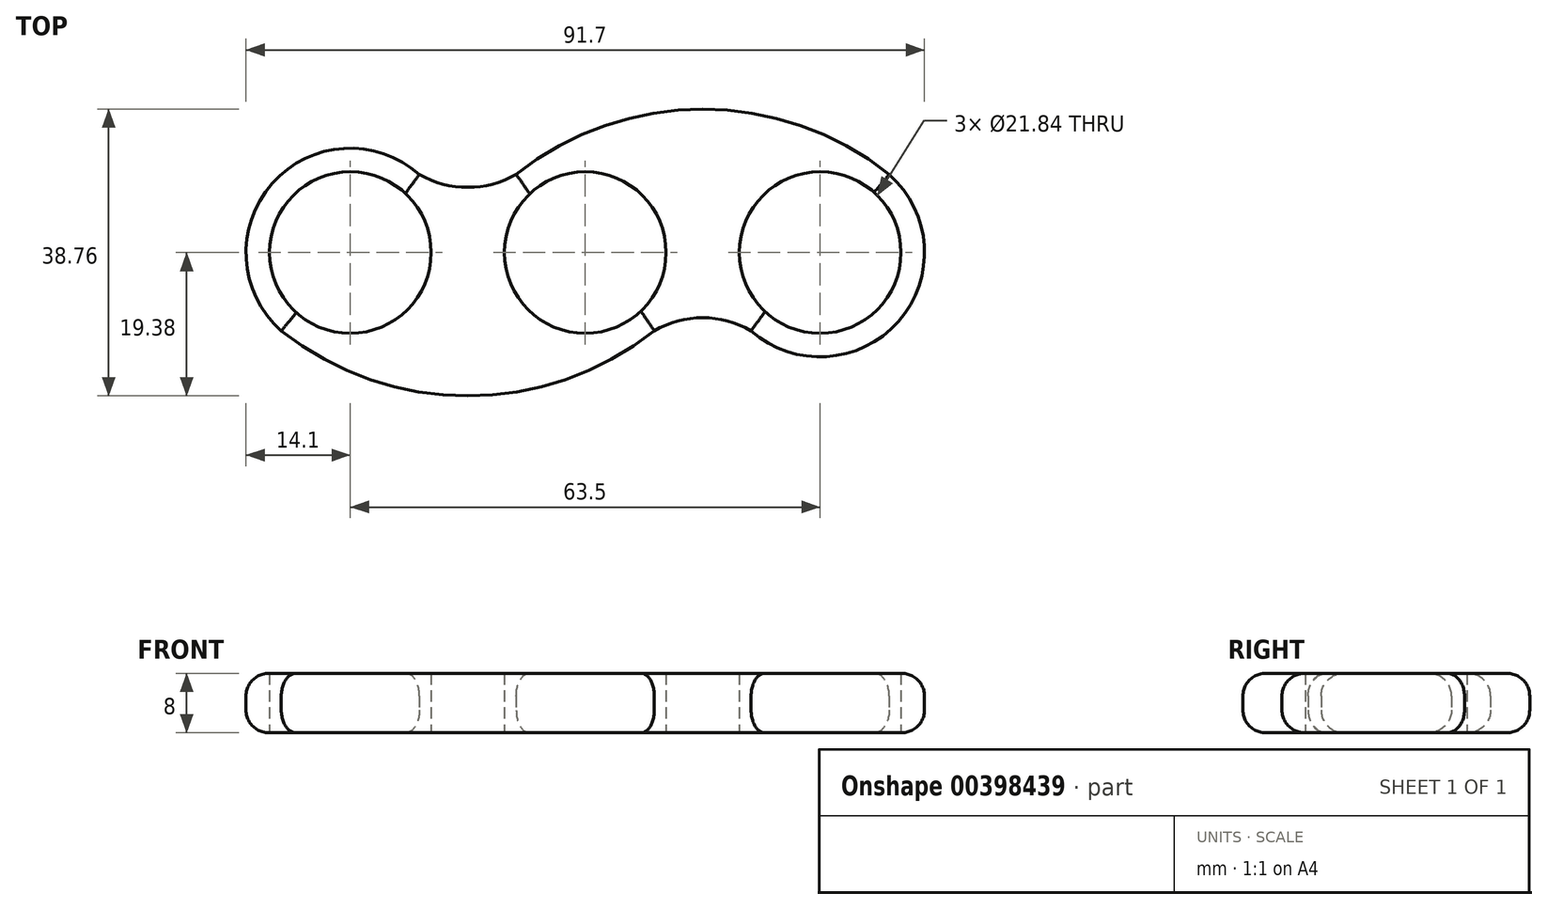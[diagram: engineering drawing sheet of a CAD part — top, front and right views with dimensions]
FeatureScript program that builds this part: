
annotation { "Feature Type Name" : "Feature", "Feature Type Description" : "" }
export const myFeature = defineFeature(function(context is Context, id is Id, definition is map)
    precondition{}
    {
        {
            var Q0;
            Q0=qCreatedBy(makeId("Top.planeOp"),FACE);
            var sketch = newSketch(context, id + "F0", { "sketchPlane" : qUnion([Q0])});
            skCircle(sketch, "E0", {"center": v(0, 0) * mm, "radius": 10.92 * mm});
            skCircle(sketch, "E1", {"center": v(0, 0) * mm, "radius": 14.1 * mm});
            skLineSegment(sketch, "E2", {"start": v(0, 0) * mm, "end": v(-31.75, 0) * mm});
            skLineSegment(sketch, "E3", {"start": v(0, 0) * mm, "end": v(31.75, 0) * mm});
            skCircle(sketch, "E4", {"center": v(31.75, 0) * mm, "radius": 10.92 * mm});
            skCircle(sketch, "E5", {"center": v(31.75, 0) * mm, "radius": 14.1 * mm});
            skCircle(sketch, "E6", {"center": v(-31.75, 0) * mm, "radius": 10.92 * mm});
            skCircle(sketch, "E7", {"center": v(-31.75, 0) * mm, "radius": 14.1 * mm});
            skPoint(sketch, "E8", {"position": v(-15.88, 0) * mm});
            skPoint(sketch, "E9", {"position": v(15.88, 0) * mm});
            skPoint(sketch, "E10", {"position": v(-15.88, 8.81) * mm});
            skPoint(sketch, "E11", {"position": v(15.88, -8.81) * mm});
            skPoint(sketch, "E12", {"position": v(-9.32, 10.57) * mm});
            skPoint(sketch, "E13", {"position": v(-22.42, 10.57) * mm});
            skArc(sketch, "E14", {"start": v(-22.42, 10.57) * mm, "mid": v(-15.87, 8.81) * mm, "end": v(-9.32, 10.57) * mm});
            skPoint(sketch, "E15", {"position": v(-41.08, -10.57) * mm});
            skPoint(sketch, "E16", {"position": v(9.33, -10.57) * mm});
            skPoint(sketch, "E17", {"position": v(41.08, 10.57) * mm});
            skPoint(sketch, "E18", {"position": v(22.42, -10.57) * mm});
            skArc(sketch, "E19", {"start": v(22.42, -10.57) * mm, "mid": v(15.88, -8.81) * mm, "end": v(9.33, -10.57) * mm});
            skPoint(sketch, "E20", {"position": v(-15.88, -19.38) * mm});
            skPoint(sketch, "E21", {"position": v(15.87, 19.38) * mm});
            skArc(sketch, "E22", {"start": v(-41.08, -10.57) * mm, "mid": v(-15.88, -19.38) * mm, "end": v(9.33, -10.57) * mm});
            skArc(sketch, "E23", {"start": v(41.08, 10.57) * mm, "mid": v(15.88, 19.38) * mm, "end": v(-9.32, 10.57) * mm});
            skSolve(sketch);
        }
        {
            var Q0;
            Q0=makeQuery(id+"F0.imprint","IMPRINT",FACE,{"disambiguationData":[TD([[makeQuery(id+"F0.imprint","IMPRINT",EDGE,{"derivedFrom":sQuery(id+"F0.wireOp",EDGE,"E6")}),-1.0]])]});
            var Q1;
            {var subQ0=sQuery(id+"F0.wireOp",EDGE,"E14");Q1=makeQuery(id+"F0.imprint","IMPRINT",FACE,{"disambiguationData":[TD([[makeQuery(id+"F0.imprint","IMPRINT",EDGE,{"derivedFrom":subQ0}),-1.0]])]});}
            var Q2;
            {var subQ0=sQuery(id+"F0.wireOp",EDGE,"E22");var subQ1=sQuery(id+"F0.wireOp",EDGE,"E1");var subQ2=makeQuery(id+"F0.imprint","INTERSECT",VERTEX,{"derivedFrom":[subQ1,subQ0]});Q2=makeQuery(id+"F0.imprint","IMPRINT",FACE,{"disambiguationData":[TD([[makeQuery(id+"F0.imprint","IMPRINT",EDGE,{"disambiguationData":[TD([[subQ2,1.0]])],"derivedFrom":subQ1}),-1.0]])]});}
            var Q3;
            {var subQ0=sQuery(id+"F0.wireOp",EDGE,"E2");var subQ1=sQuery(id+"F0.wireOp",EDGE,"E0");var subQ2=makeQuery(id+"F0.imprint","INTERSECT",VERTEX,{"derivedFrom":[subQ1,subQ0]});Q3=makeQuery(id+"F0.imprint","IMPRINT",FACE,{"disambiguationData":[TD([[makeQuery(id+"F0.imprint","IMPRINT",EDGE,{"disambiguationData":[TD([[subQ2,-1.0]])],"derivedFrom":subQ1}),-1.0]])]});}
            var Q4;
            {var subQ0=sQuery(id+"F0.wireOp",EDGE,"E2");var subQ1=sQuery(id+"F0.wireOp",EDGE,"E0");var subQ2=makeQuery(id+"F0.imprint","INTERSECT",VERTEX,{"derivedFrom":[subQ1,subQ0]});Q4=makeQuery(id+"F0.imprint","IMPRINT",FACE,{"disambiguationData":[TD([[makeQuery(id+"F0.imprint","IMPRINT",EDGE,{"disambiguationData":[TD([[subQ2,1.0]])],"derivedFrom":subQ1}),-1.0]])]});}
            var Q5;
            {var subQ0=sQuery(id+"F0.wireOp",EDGE,"E23");var subQ1=sQuery(id+"F0.wireOp",EDGE,"E1");var subQ2=makeQuery(id+"F0.imprint","INTERSECT",VERTEX,{"derivedFrom":[subQ1,subQ0]});Q5=makeQuery(id+"F0.imprint","IMPRINT",FACE,{"disambiguationData":[TD([[makeQuery(id+"F0.imprint","IMPRINT",EDGE,{"disambiguationData":[TD([[subQ2,1.0]])],"derivedFrom":subQ1}),-1.0]])]});}
            var Q6;
            {var subQ0=sQuery(id+"F0.wireOp",EDGE,"E19");Q6=makeQuery(id+"F0.imprint","IMPRINT",FACE,{"disambiguationData":[TD([[makeQuery(id+"F0.imprint","IMPRINT",EDGE,{"derivedFrom":subQ0}),-1.0]])]});}
            var Q7;
            Q7=makeQuery(id+"F0.imprint","IMPRINT",FACE,{"disambiguationData":[TD([[makeQuery(id+"F0.imprint","IMPRINT",EDGE,{"derivedFrom":sQuery(id+"F0.wireOp",EDGE,"E4")}),-1.0]])]});
            extrude(context, id + "F1", {"entities" : qUnion([Q0, Q1, Q2, Q3, Q4, Q5, Q6, Q7]), "depth" : 8 * mm});
        }
        {
            var Q0;
            Q0=makeQuery(id+"F1.opExtrude","CAP_EDGE",EDGE,{"disambiguationData":[OSD([sQuery(id+"F0.wireOp",EDGE,"E22")])],"isStart":false});
            var Q1;
            Q1=makeQuery(id+"F1.opExtrude","CAP_EDGE",EDGE,{"disambiguationData":[OSD([sQuery(id+"F0.wireOp",EDGE,"E19")])],"isStart":false});
            var Q2;
            Q2=makeQuery(id+"F1.opExtrude","CAP_EDGE",EDGE,{"disambiguationData":[OSD([sQuery(id+"F0.wireOp",EDGE,"E5")])],"isStart":false});
            var Q3;
            Q3=makeQuery(id+"F1.opExtrude","CAP_EDGE",EDGE,{"disambiguationData":[OSD([sQuery(id+"F0.wireOp",EDGE,"E23")])],"isStart":false});
            var Q4;
            Q4=makeQuery(id+"F1.opExtrude","CAP_EDGE",EDGE,{"disambiguationData":[OSD([sQuery(id+"F0.wireOp",EDGE,"E14")])],"isStart":false});
            var Q5;
            Q5=makeQuery(id+"F1.opExtrude","CAP_EDGE",EDGE,{"disambiguationData":[OSD([sQuery(id+"F0.wireOp",EDGE,"E7")])],"isStart":false});
            fillet(context, id + "F2", {"entities" : qUnion([Q0, Q1, Q2, Q3, Q4, Q5]), "radius" : 3.05 * mm, "tangentPropagation" : true, "allowEdgeOverflow" : false});
        }
        {
            var Q0;
            Q0=makeQuery(id+"F1.opExtrude","CAP_EDGE",EDGE,{"disambiguationData":[OSD([sQuery(id+"F0.wireOp",EDGE,"E22")])],"isStart":true});
            var Q1;
            Q1=makeQuery(id+"F1.opExtrude","CAP_EDGE",EDGE,{"disambiguationData":[OSD([sQuery(id+"F0.wireOp",EDGE,"E19")])],"isStart":true});
            var Q2;
            Q2=makeQuery(id+"F1.opExtrude","CAP_EDGE",EDGE,{"disambiguationData":[OSD([sQuery(id+"F0.wireOp",EDGE,"E5")])],"isStart":true});
            var Q3;
            Q3=makeQuery(id+"F1.opExtrude","CAP_EDGE",EDGE,{"disambiguationData":[OSD([sQuery(id+"F0.wireOp",EDGE,"E23")])],"isStart":true});
            var Q4;
            Q4=makeQuery(id+"F1.opExtrude","CAP_EDGE",EDGE,{"disambiguationData":[OSD([sQuery(id+"F0.wireOp",EDGE,"E14")])],"isStart":true});
            var Q5;
            Q5=makeQuery(id+"F1.opExtrude","CAP_EDGE",EDGE,{"disambiguationData":[OSD([sQuery(id+"F0.wireOp",EDGE,"E7")])],"isStart":true});
            fillet(context, id + "F3", {"entities" : qUnion([Q0, Q1, Q2, Q3, Q4, Q5]), "radius" : 3.05 * mm, "tangentPropagation" : true, "allowEdgeOverflow" : false});
        }
    });
